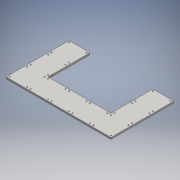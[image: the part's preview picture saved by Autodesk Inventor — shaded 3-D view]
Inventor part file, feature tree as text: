
AUTODESK INVENTOR PART (.ipt)
format: ipt  version: 2016 (Build 200138000, 138)  size: 207,360 bytes
history: native  units: mm
features: extrude x1, sketch x1
ambient origin geometry x8: Origin, YZ Plane, XZ Plane, XY Plane, X Axis, Y Axis, Z Axis, Center Point
bodies: Solid1 (feature_tree)
feature tree (2):
  extrude  "Extrusion1"  Depth=60.0mm
  sketch  "Sketch1"  dims[d0=180.0mm d1=60.0mm d2=120.0mm d3=180.0mm d4=60.0mm d5=60.0mm d6=60.0mm d7=60.0mm d8=60.0mm d9=50.0mm d10=50.0mm d11=50.0mm d12=50.0mm d13=50.0mm d14=50.0mm d15=50.0mm d16=50.0mm d17=50.0mm d18=50.0mm d19=50.0mm d20=50.0mm d21=50.0mm d22=50.0mm d23=50.0mm d24=50.0mm d25=50.0mm d26=50.0mm d27=3.0mm d28=3.0mm d29=3.0mm d30=3.0mm d31=3.0mm d32=3.0mm d33=3.0mm d34=3.0mm d35=3.0mm d36=3.0mm d37=3.0mm d38=3.0mm d39=3.0mm d40=3.0mm d41=3.0mm d42=3.0mm d43=3.0mm d44=3.0mm d45=3.0mm d46=3.0mm d47=3.0mm d48=3.0mm d49=3.0mm d50=3.0mm d51=3.0mm d52=3.0mm d53=3.0mm d54=3.0mm d55=3.0mm d56=3.0mm d57=3.0mm d58=3.0mm d59=3.0mm d60=3.0mm d61=3.0mm d62=3.0mm d63=5.0mm d64=0.0mm]
